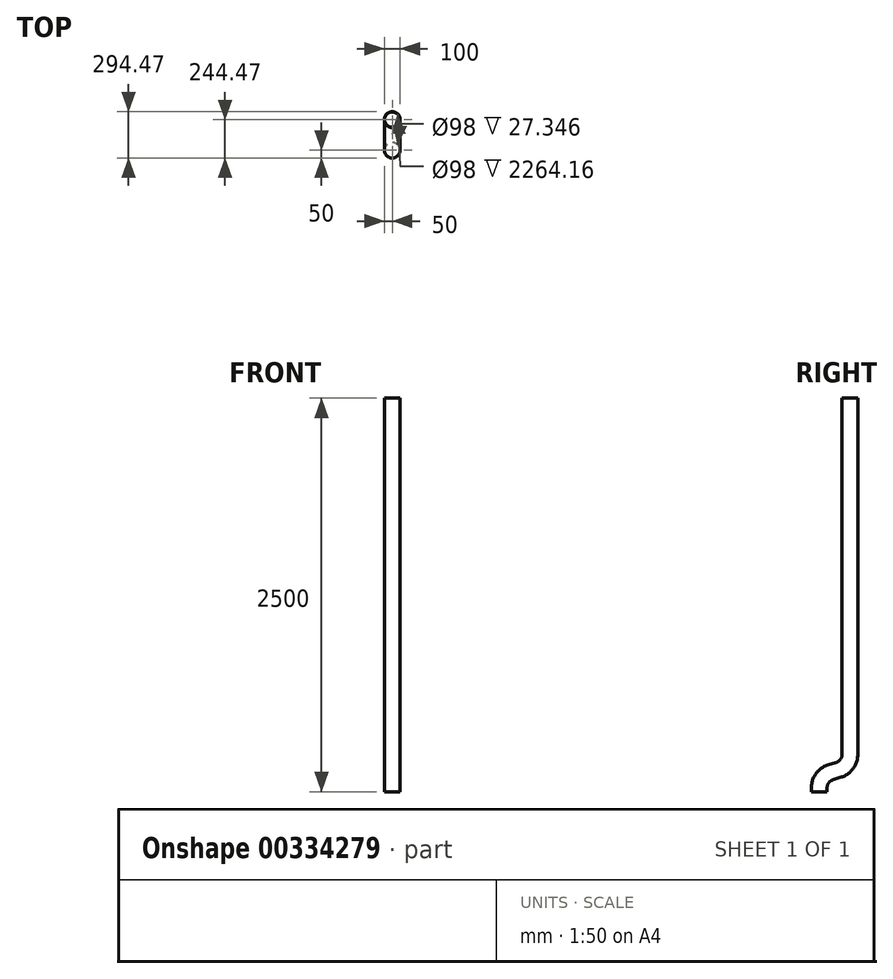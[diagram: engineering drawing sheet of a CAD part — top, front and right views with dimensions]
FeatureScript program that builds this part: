
annotation { "Feature Type Name" : "Feature", "Feature Type Description" : "" }
export const myFeature = defineFeature(function(context is Context, id is Id, definition is map)
    precondition{}
    {
        {
            var Q0;
            Q0=qCreatedBy(makeId("Right.planeOp"),FACE);
            var sketch = newSketch(context, id + "F0", { "sketchPlane" : qUnion([Q0])});
            skLineSegment(sketch, "E0", {"start": v(0, 0) * mm, "end": v(0, -2264.16) * mm});
            skLineSegment(sketch, "E1", {"start": v(-69.1, -2359.26) * mm, "end": v(-125.37, -2377.55) * mm});
            skLineSegment(sketch, "E2", {"start": v(-194.47, -2472.65) * mm, "end": v(-194.47, -2500) * mm});
            skPoint(sketch, "E3.visualSharp", {"position": v(0, -2336.81) * mm});
            skArc(sketch, "E3.filletArc", {"start": v(-69.1, -2359.26) * mm, "mid": v(-19.1, -2322.94) * mm, "end": v(0, -2264.16) * mm});
            skPoint(sketch, "E4.visualSharp", {"position": v(-194.47, -2400) * mm});
            skArc(sketch, "E4.filletArc", {"start": v(-125.37, -2377.55) * mm, "mid": v(-175.37, -2413.88) * mm, "end": v(-194.47, -2472.65) * mm});
            skSolve(sketch);
        }
        {
            var Q0;
            Q0=qCreatedBy(makeId("Top.planeOp"),FACE);
            var sketch = newSketch(context, id + "F1", { "sketchPlane" : qUnion([Q0])});
            skCircle(sketch, "E5", {"center": v(0, 0) * mm, "radius": 50 * mm});
            skCircle(sketch, "E6", {"center": v(0, 0) * mm, "radius": 49 * mm});
            skSolve(sketch);
        }
        {
            var Q0;
            Q0=makeQuery(id+"F1.imprint","IMPRINT",FACE,{"disambiguationData":[TD([[makeQuery(id+"F1.imprint","IMPRINT",EDGE,{"derivedFrom":sQuery(id+"F1.wireOp",EDGE,"E5")}),1.0]])]});
            var Q1;
            Q1=sQuery(id+"F0.wireOp",EDGE,"E0");
            var Q2;
            Q2=sQuery(id+"F0.wireOp",EDGE,"E3.filletArc");
            var Q3;
            Q3=sQuery(id+"F0.wireOp",EDGE,"E1");
            var Q4;
            Q4=sQuery(id+"F0.wireOp",EDGE,"E4.filletArc");
            var Q5;
            Q5=sQuery(id+"F0.wireOp",EDGE,"E2");
            sweep(context, id + "F2", {"profiles" : qUnion([Q0]), "path" : qUnion([Q1, Q2, Q3, Q4, Q5])});
        }
    });
